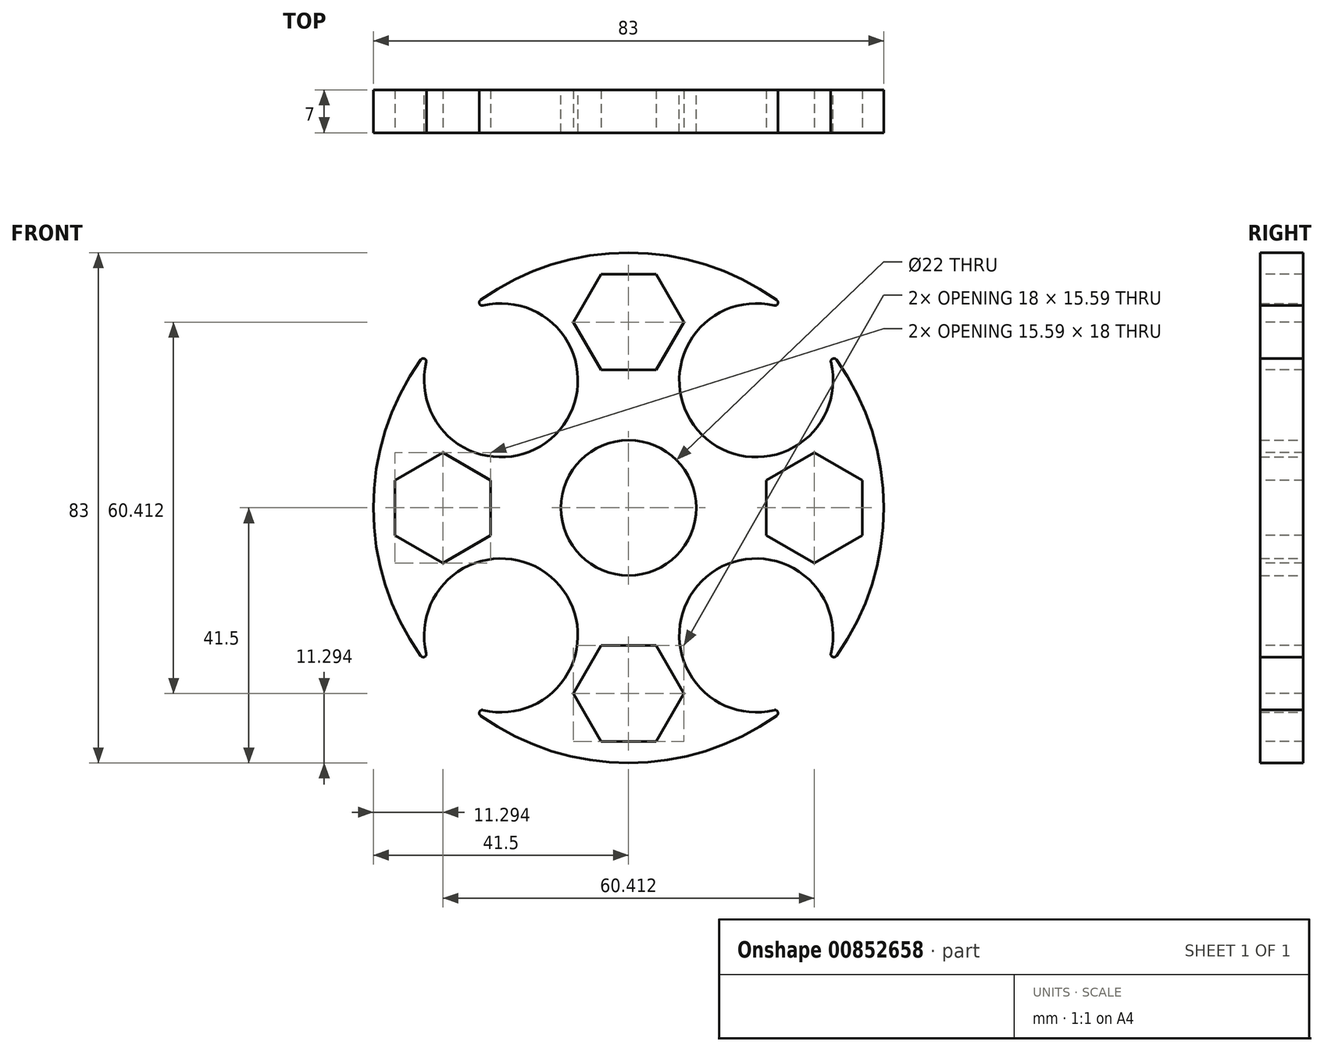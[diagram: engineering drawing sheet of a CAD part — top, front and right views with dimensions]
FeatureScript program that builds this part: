
annotation { "Feature Type Name" : "Feature", "Feature Type Description" : "" }
export const myFeature = defineFeature(function(context is Context, id is Id, definition is map)
    precondition{}
    {
        {
            var Q0;
            Q0=qCreatedBy(makeId("Front.planeOp"),FACE);
            var sketch = newSketch(context, id + "F0", { "sketchPlane" : qUnion([Q0])});
            skCircle(sketch, "E0", {"center": v(0, 0) * mm, "radius": 11 * mm});
            skCircle(sketch, "E1", {"center": v(0, 0) * mm, "radius": 41.5 * mm});
            skLineSegment(sketch, "E2", {"start": v(0, 0) * mm, "end": v(0, 41.5) * mm});
            skLineSegment(sketch, "E3", {"start": v(0, 0) * mm, "end": v(41.5, 0) * mm});
            skLineSegment(sketch, "E4", {"start": v(0, 0) * mm, "end": v(0, -41.5) * mm});
            skLineSegment(sketch, "E5", {"start": v(0, 0) * mm, "end": v(-41.5, 0) * mm});
            skLineSegment(sketch, "E6", {"start": v(-20.75, 0) * mm, "end": v(-20.75, 35.94) * mm});
            skLineSegment(sketch, "E7", {"start": v(0, 20.75) * mm, "end": v(-35.94, 20.75) * mm});
            skLineSegment(sketch, "E8", {"start": v(0, 20.75) * mm, "end": v(35.94, 20.75) * mm});
            skLineSegment(sketch, "E9", {"start": v(20.75, 0) * mm, "end": v(20.75, 35.94) * mm});
            skLineSegment(sketch, "E10", {"start": v(0, -20.75) * mm, "end": v(35.94, -20.75) * mm});
            skLineSegment(sketch, "E11", {"start": v(20.75, 0) * mm, "end": v(20.75, -35.94) * mm});
            skLineSegment(sketch, "E12", {"start": v(-20.75, 0) * mm, "end": v(-20.75, -35.94) * mm});
            skLineSegment(sketch, "E13", {"start": v(0, -20.75) * mm, "end": v(-35.94, -20.75) * mm});
            skCircle(sketch, "E14", {"center": v(-20.75, 20.75) * mm, "radius": 12.5 * mm});
            skCircle(sketch, "E15", {"center": v(20.75, 20.75) * mm, "radius": 12.5 * mm});
            skCircle(sketch, "E16", {"center": v(-20.75, -20.75) * mm, "radius": 12.5 * mm});
            skCircle(sketch, "E17", {"center": v(20.75, -20.75) * mm, "radius": 12.5 * mm});
            skSolve(sketch);
        }
        {
            var Q0;
            {var subQ1=sQuery(id+"F0.wireOp",EDGE,"E2");var subQ5=sQuery(id+"F0.wireOp",EDGE,"E1");var subQ6=makeQuery(id+"F0.imprint","INTERSECT",VERTEX,{"derivedFrom":[subQ5,subQ1]});Q0=makeQuery(id+"F0.imprint","IMPRINT",FACE,{"disambiguationData":[TD([[makeQuery(id+"F0.imprint","IMPRINT",EDGE,{"disambiguationData":[TD([[subQ6,-1.0]])],"derivedFrom":subQ5}),1.0]])]});}
            var Q1;
            {var subQ1=sQuery(id+"F0.wireOp",EDGE,"E2");var subQ7=sQuery(id+"F0.wireOp",EDGE,"E1");var subQ9=makeQuery(id+"F0.imprint","INTERSECT",VERTEX,{"derivedFrom":[subQ7,subQ1]});Q1=makeQuery(id+"F0.imprint","IMPRINT",FACE,{"disambiguationData":[TD([[makeQuery(id+"F0.imprint","IMPRINT",EDGE,{"disambiguationData":[TD([[subQ9,1.0]])],"derivedFrom":subQ7}),1.0]])]});}
            var Q2;
            {var subQ3=sQuery(id+"F0.wireOp",EDGE,"E0");var subQ5=sQuery(id+"F0.wireOp",EDGE,"E2");var subQ6=makeQuery(id+"F0.imprint","INTERSECT",VERTEX,{"derivedFrom":[subQ3,subQ5]});Q2=makeQuery(id+"F0.imprint","IMPRINT",FACE,{"disambiguationData":[TD([[makeQuery(id+"F0.imprint","IMPRINT",EDGE,{"disambiguationData":[TD([[subQ6,-1.0]])],"derivedFrom":subQ3}),-1.0]])]});}
            var Q3;
            {var subQ1=sQuery(id+"F0.wireOp",EDGE,"E2");var subQ5=sQuery(id+"F0.wireOp",EDGE,"E0");var subQ6=makeQuery(id+"F0.imprint","INTERSECT",VERTEX,{"derivedFrom":[subQ5,subQ1]});Q3=makeQuery(id+"F0.imprint","IMPRINT",FACE,{"disambiguationData":[TD([[makeQuery(id+"F0.imprint","IMPRINT",EDGE,{"disambiguationData":[TD([[subQ6,1.0]])],"derivedFrom":subQ5}),-1.0]])]});}
            var Q4;
            {var subQ1=sQuery(id+"F0.wireOp",EDGE,"E3");var subQ5=sQuery(id+"F0.wireOp",EDGE,"E1");var subQ6=makeQuery(id+"F0.imprint","INTERSECT",VERTEX,{"derivedFrom":[subQ5,subQ1]});Q4=makeQuery(id+"F0.imprint","IMPRINT",FACE,{"disambiguationData":[TD([[makeQuery(id+"F0.imprint","IMPRINT",EDGE,{"disambiguationData":[TD([[subQ6,-1.0]])],"derivedFrom":subQ5}),1.0]])]});}
            var Q5;
            {var subQ1=sQuery(id+"F0.wireOp",EDGE,"E5");var subQ5=sQuery(id+"F0.wireOp",EDGE,"E1");var subQ6=makeQuery(id+"F0.imprint","INTERSECT",VERTEX,{"derivedFrom":[subQ5,subQ1]});Q5=makeQuery(id+"F0.imprint","IMPRINT",FACE,{"disambiguationData":[TD([[makeQuery(id+"F0.imprint","IMPRINT",EDGE,{"disambiguationData":[TD([[subQ6,1.0]])],"derivedFrom":subQ5}),1.0]])]});}
            var Q6;
            {var subQ1=sQuery(id+"F0.wireOp",EDGE,"E1");var subQ6=sQuery(id+"F0.wireOp",EDGE,"E5");var subQ9=makeQuery(id+"F0.imprint","INTERSECT",VERTEX,{"derivedFrom":[subQ1,subQ6]});Q6=makeQuery(id+"F0.imprint","IMPRINT",FACE,{"disambiguationData":[TD([[makeQuery(id+"F0.imprint","IMPRINT",EDGE,{"disambiguationData":[TD([[subQ9,-1.0]])],"derivedFrom":subQ1}),1.0]])]});}
            var Q7;
            {var subQ1=sQuery(id+"F0.wireOp",EDGE,"E5");var subQ5=sQuery(id+"F0.wireOp",EDGE,"E0");var subQ6=makeQuery(id+"F0.imprint","INTERSECT",VERTEX,{"derivedFrom":[subQ5,subQ1]});Q7=makeQuery(id+"F0.imprint","IMPRINT",FACE,{"disambiguationData":[TD([[makeQuery(id+"F0.imprint","IMPRINT",EDGE,{"disambiguationData":[TD([[subQ6,-1.0]])],"derivedFrom":subQ5}),-1.0]])]});}
            var Q8;
            {var subQ1=sQuery(id+"F0.wireOp",EDGE,"E4");var subQ5=sQuery(id+"F0.wireOp",EDGE,"E1");var subQ6=makeQuery(id+"F0.imprint","INTERSECT",VERTEX,{"derivedFrom":[subQ5,subQ1]});Q8=makeQuery(id+"F0.imprint","IMPRINT",FACE,{"disambiguationData":[TD([[makeQuery(id+"F0.imprint","IMPRINT",EDGE,{"disambiguationData":[TD([[subQ6,1.0]])],"derivedFrom":subQ5}),1.0]])]});}
            var Q9;
            {var subQ1=sQuery(id+"F0.wireOp",EDGE,"E4");var subQ5=sQuery(id+"F0.wireOp",EDGE,"E1");var subQ6=makeQuery(id+"F0.imprint","INTERSECT",VERTEX,{"derivedFrom":[subQ5,subQ1]});Q9=makeQuery(id+"F0.imprint","IMPRINT",FACE,{"disambiguationData":[TD([[makeQuery(id+"F0.imprint","IMPRINT",EDGE,{"disambiguationData":[TD([[subQ6,-1.0]])],"derivedFrom":subQ5}),1.0]])]});}
            var Q10;
            {var subQ5=sQuery(id+"F0.wireOp",EDGE,"E0");var subQ8=sQuery(id+"F0.wireOp",EDGE,"E3");var subQ10=makeQuery(id+"F0.imprint","INTERSECT",VERTEX,{"derivedFrom":[subQ5,subQ8]});Q10=makeQuery(id+"F0.imprint","IMPRINT",FACE,{"disambiguationData":[TD([[makeQuery(id+"F0.imprint","IMPRINT",EDGE,{"disambiguationData":[TD([[subQ10,1.0]])],"derivedFrom":subQ5}),-1.0]])]});}
            var Q11;
            {var subQ1=sQuery(id+"F0.wireOp",EDGE,"E3");var subQ5=sQuery(id+"F0.wireOp",EDGE,"E1");var subQ6=makeQuery(id+"F0.imprint","INTERSECT",VERTEX,{"derivedFrom":[subQ5,subQ1]});Q11=makeQuery(id+"F0.imprint","IMPRINT",FACE,{"disambiguationData":[TD([[makeQuery(id+"F0.imprint","IMPRINT",EDGE,{"disambiguationData":[TD([[subQ6,1.0]])],"derivedFrom":subQ5}),1.0]])]});}
            var Q12;
            {var subQ0=sQuery(id+"F0.wireOp",EDGE,"E11");var subQ1=sQuery(id+"F0.wireOp",EDGE,"E1");var subQ2=makeQuery(id+"F0.imprint","INTERSECT",VERTEX,{"derivedFrom":[subQ1,subQ0]});Q12=makeQuery(id+"F0.imprint","IMPRINT",FACE,{"disambiguationData":[TD([[makeQuery(id+"F0.imprint","IMPRINT",EDGE,{"disambiguationData":[TD([[subQ2,-1.0]])],"derivedFrom":subQ1}),1.0]])]});}
            var Q13;
            {var subQ0=sQuery(id+"F0.wireOp",EDGE,"E10");var subQ1=sQuery(id+"F0.wireOp",EDGE,"E1");var subQ2=makeQuery(id+"F0.imprint","INTERSECT",VERTEX,{"derivedFrom":[subQ1,subQ0]});Q13=makeQuery(id+"F0.imprint","IMPRINT",FACE,{"disambiguationData":[TD([[makeQuery(id+"F0.imprint","IMPRINT",EDGE,{"disambiguationData":[TD([[subQ2,1.0]])],"derivedFrom":subQ1}),1.0]])]});}
            var Q14;
            {var subQ0=sQuery(id+"F0.wireOp",EDGE,"E12");var subQ1=sQuery(id+"F0.wireOp",EDGE,"E1");var subQ2=makeQuery(id+"F0.imprint","INTERSECT",VERTEX,{"derivedFrom":[subQ1,subQ0]});Q14=makeQuery(id+"F0.imprint","IMPRINT",FACE,{"disambiguationData":[TD([[makeQuery(id+"F0.imprint","IMPRINT",EDGE,{"disambiguationData":[TD([[subQ2,1.0]])],"derivedFrom":subQ1}),1.0]])]});}
            var Q15;
            {var subQ0=sQuery(id+"F0.wireOp",EDGE,"E13");var subQ1=sQuery(id+"F0.wireOp",EDGE,"E1");var subQ2=makeQuery(id+"F0.imprint","INTERSECT",VERTEX,{"derivedFrom":[subQ1,subQ0]});Q15=makeQuery(id+"F0.imprint","IMPRINT",FACE,{"disambiguationData":[TD([[makeQuery(id+"F0.imprint","IMPRINT",EDGE,{"disambiguationData":[TD([[subQ2,-1.0]])],"derivedFrom":subQ1}),1.0]])]});}
            var Q16;
            {var subQ0=sQuery(id+"F0.wireOp",EDGE,"E7");var subQ1=sQuery(id+"F0.wireOp",EDGE,"E1");var subQ2=makeQuery(id+"F0.imprint","INTERSECT",VERTEX,{"derivedFrom":[subQ1,subQ0]});Q16=makeQuery(id+"F0.imprint","IMPRINT",FACE,{"disambiguationData":[TD([[makeQuery(id+"F0.imprint","IMPRINT",EDGE,{"disambiguationData":[TD([[subQ2,1.0]])],"derivedFrom":subQ1}),1.0]])]});}
            var Q17;
            {var subQ0=sQuery(id+"F0.wireOp",EDGE,"E6");var subQ1=sQuery(id+"F0.wireOp",EDGE,"E1");var subQ2=makeQuery(id+"F0.imprint","INTERSECT",VERTEX,{"derivedFrom":[subQ1,subQ0]});Q17=makeQuery(id+"F0.imprint","IMPRINT",FACE,{"disambiguationData":[TD([[makeQuery(id+"F0.imprint","IMPRINT",EDGE,{"disambiguationData":[TD([[subQ2,-1.0]])],"derivedFrom":subQ1}),1.0]])]});}
            var Q18;
            {var subQ0=sQuery(id+"F0.wireOp",EDGE,"E9");var subQ1=sQuery(id+"F0.wireOp",EDGE,"E1");var subQ2=makeQuery(id+"F0.imprint","INTERSECT",VERTEX,{"derivedFrom":[subQ1,subQ0]});Q18=makeQuery(id+"F0.imprint","IMPRINT",FACE,{"disambiguationData":[TD([[makeQuery(id+"F0.imprint","IMPRINT",EDGE,{"disambiguationData":[TD([[subQ2,1.0]])],"derivedFrom":subQ1}),1.0]])]});}
            var Q19;
            {var subQ0=sQuery(id+"F0.wireOp",EDGE,"E8");var subQ1=sQuery(id+"F0.wireOp",EDGE,"E1");var subQ2=makeQuery(id+"F0.imprint","INTERSECT",VERTEX,{"derivedFrom":[subQ1,subQ0]});Q19=makeQuery(id+"F0.imprint","IMPRINT",FACE,{"disambiguationData":[TD([[makeQuery(id+"F0.imprint","IMPRINT",EDGE,{"disambiguationData":[TD([[subQ2,-1.0]])],"derivedFrom":subQ1}),1.0]])]});}
            extrude(context, id + "F1", {"entities" : qUnion([Q0, Q1, Q2, Q3, Q4, Q5, Q6, Q7, Q8, Q9, Q10, Q11, Q12, Q13, Q14, Q15, Q16, Q17, Q18, Q19]), "depth" : 7 * mm, "offsetDistance" : 25 * mm});
        }
        {
            var Q0;
            {var subQ0=sQuery(id+"F0.wireOp",EDGE,"E15");var subQ1=sQuery(id+"F0.wireOp",EDGE,"E1");Q0=makeQuery(id+"F1.opExtrude","SWEPT_EDGE",EDGE,{"disambiguationData":[OSD([subQ1,subQ0]),TDD([makeQuery(id+"F0.imprint","INTERSECT",VERTEX,{"disambiguationData":[OD(1.0)],"derivedFrom":[subQ1,subQ0]})])]});}
            var Q1;
            {var subQ0=sQuery(id+"F0.wireOp",EDGE,"E15");var subQ1=sQuery(id+"F0.wireOp",EDGE,"E1");Q1=makeQuery(id+"F1.opExtrude","SWEPT_EDGE",EDGE,{"disambiguationData":[OSD([subQ1,subQ0]),TDD([makeQuery(id+"F0.imprint","INTERSECT",VERTEX,{"disambiguationData":[OD(0.0)],"derivedFrom":[subQ1,subQ0]})])]});}
            var Q2;
            {var subQ0=sQuery(id+"F0.wireOp",EDGE,"E17");var subQ1=sQuery(id+"F0.wireOp",EDGE,"E1");Q2=makeQuery(id+"F1.opExtrude","SWEPT_EDGE",EDGE,{"disambiguationData":[OSD([subQ1,subQ0]),TDD([makeQuery(id+"F0.imprint","INTERSECT",VERTEX,{"disambiguationData":[OD(1.0)],"derivedFrom":[subQ1,subQ0]})])]});}
            var Q3;
            {var subQ0=sQuery(id+"F0.wireOp",EDGE,"E17");var subQ1=sQuery(id+"F0.wireOp",EDGE,"E1");Q3=makeQuery(id+"F1.opExtrude","SWEPT_EDGE",EDGE,{"disambiguationData":[OSD([subQ1,subQ0]),TDD([makeQuery(id+"F0.imprint","INTERSECT",VERTEX,{"disambiguationData":[OD(0.0)],"derivedFrom":[subQ1,subQ0]})])]});}
            var Q4;
            {var subQ0=sQuery(id+"F0.wireOp",EDGE,"E16");var subQ1=sQuery(id+"F0.wireOp",EDGE,"E1");Q4=makeQuery(id+"F1.opExtrude","SWEPT_EDGE",EDGE,{"disambiguationData":[OSD([subQ1,subQ0]),TDD([makeQuery(id+"F0.imprint","INTERSECT",VERTEX,{"disambiguationData":[OD(1.0)],"derivedFrom":[subQ1,subQ0]})])]});}
            var Q5;
            {var subQ0=sQuery(id+"F0.wireOp",EDGE,"E16");var subQ1=sQuery(id+"F0.wireOp",EDGE,"E1");Q5=makeQuery(id+"F1.opExtrude","SWEPT_EDGE",EDGE,{"disambiguationData":[OSD([subQ1,subQ0]),TDD([makeQuery(id+"F0.imprint","INTERSECT",VERTEX,{"disambiguationData":[OD(0.0)],"derivedFrom":[subQ1,subQ0]})])]});}
            var Q6;
            {var subQ0=sQuery(id+"F0.wireOp",EDGE,"E14");var subQ1=sQuery(id+"F0.wireOp",EDGE,"E1");Q6=makeQuery(id+"F1.opExtrude","SWEPT_EDGE",EDGE,{"disambiguationData":[OSD([subQ1,subQ0]),TDD([makeQuery(id+"F0.imprint","INTERSECT",VERTEX,{"disambiguationData":[OD(0.0)],"derivedFrom":[subQ1,subQ0]})])]});}
            var Q7;
            {var subQ0=sQuery(id+"F0.wireOp",EDGE,"E14");var subQ1=sQuery(id+"F0.wireOp",EDGE,"E1");Q7=makeQuery(id+"F1.opExtrude","SWEPT_EDGE",EDGE,{"disambiguationData":[OSD([subQ1,subQ0]),TDD([makeQuery(id+"F0.imprint","INTERSECT",VERTEX,{"disambiguationData":[OD(1.0)],"derivedFrom":[subQ1,subQ0]})])]});}
            fillet(context, id + "F2", {"entities" : qUnion([Q0, Q1, Q2, Q3, Q4, Q5, Q6, Q7]), "radius" : 0.5 * mm, "tangentPropagation" : true, "allowEdgeOverflow" : false});
        }
        {
            var Q0;
            Q0=makeQuery(id+"F1.opExtrude","CAP_FACE",FACE,{"disambiguationData":[OSD([sQuery(id+"F0.wireOp",EDGE,"E0"),sQuery(id+"F0.wireOp",EDGE,"E1"),sQuery(id+"F0.wireOp",EDGE,"E14"),sQuery(id+"F0.wireOp",EDGE,"E15"),sQuery(id+"F0.wireOp",EDGE,"E16"),sQuery(id+"F0.wireOp",EDGE,"E17")])],"isStart":false});
            var sketch = newSketch(context, id + "F3", { "sketchPlane" : qUnion([Q0])});
            skLineSegment(sketch, "E18", {"start": v(-4.5, 38) * mm, "end": v(4.5, 38) * mm});
            skLineSegment(sketch, "E19", {"start": v(4.5, 38) * mm, "end": v(9, 30.2) * mm});
            skLineSegment(sketch, "E20", {"start": v(9, 30.2) * mm, "end": v(4.5, 22.41) * mm});
            skLineSegment(sketch, "E21", {"start": v(4.5, 22.41) * mm, "end": v(-4.5, 22.41) * mm});
            skLineSegment(sketch, "E22", {"start": v(-4.5, 22.41) * mm, "end": v(-9, 30.2) * mm});
            skLineSegment(sketch, "E23", {"start": v(-9, 30.2) * mm, "end": v(-4.5, 38) * mm});
            skLineSegment(sketch, "E24", {"start": v(0, 38) * mm, "end": v(0, 22.41) * mm});
            skLineSegment(sketch, "E25", {"start": v(38, 4.5) * mm, "end": v(38, -4.5) * mm});
            skLineSegment(sketch, "E26", {"start": v(38, -4.5) * mm, "end": v(30.2, -9) * mm});
            skLineSegment(sketch, "E27", {"start": v(30.2, -9) * mm, "end": v(22.41, -4.5) * mm});
            skLineSegment(sketch, "E28", {"start": v(22.41, -4.5) * mm, "end": v(22.41, 4.5) * mm});
            skLineSegment(sketch, "E29", {"start": v(22.41, 4.5) * mm, "end": v(30.2, 9) * mm});
            skLineSegment(sketch, "E30", {"start": v(30.2, 9) * mm, "end": v(38, 4.5) * mm});
            skLineSegment(sketch, "E31", {"start": v(38, 0) * mm, "end": v(22.41, 0) * mm});
            skLineSegment(sketch, "E32", {"start": v(-22.41, 4.5) * mm, "end": v(-22.41, -4.5) * mm});
            skLineSegment(sketch, "E33", {"start": v(-22.41, -4.5) * mm, "end": v(-30.2, -9) * mm});
            skLineSegment(sketch, "E34", {"start": v(-30.2, -9) * mm, "end": v(-38, -4.5) * mm});
            skLineSegment(sketch, "E35", {"start": v(-38, -4.5) * mm, "end": v(-38, 4.5) * mm});
            skLineSegment(sketch, "E36", {"start": v(-38, 4.5) * mm, "end": v(-30.2, 9) * mm});
            skLineSegment(sketch, "E37", {"start": v(-30.2, 9) * mm, "end": v(-22.41, 4.5) * mm});
            skLineSegment(sketch, "E38", {"start": v(-22.41, 0) * mm, "end": v(-38, 0) * mm});
            skLineSegment(sketch, "E39", {"start": v(-4.5, -22.41) * mm, "end": v(4.5, -22.41) * mm});
            skLineSegment(sketch, "E40", {"start": v(4.5, -22.41) * mm, "end": v(9, -30.2) * mm});
            skLineSegment(sketch, "E41", {"start": v(9, -30.2) * mm, "end": v(4.5, -38) * mm});
            skLineSegment(sketch, "E42", {"start": v(4.5, -38) * mm, "end": v(-4.5, -38) * mm});
            skLineSegment(sketch, "E43", {"start": v(-4.5, -38) * mm, "end": v(-9, -30.2) * mm});
            skLineSegment(sketch, "E44", {"start": v(-9, -30.2) * mm, "end": v(-4.5, -22.41) * mm});
            skLineSegment(sketch, "E45", {"start": v(0, -22.41) * mm, "end": v(0, -38) * mm});
            skSolve(sketch);
        }
        {
            var Q0;
            {var subQ1=sQuery(id+"F3.wireOp",EDGE,"E36");Q0=makeQuery(id+"F3.imprint","IMPRINT",FACE,{"disambiguationData":[TD([[makeQuery(id+"F3.imprint","IMPRINT",EDGE,{"derivedFrom":subQ1}),-1.0]])]});}
            var Q1;
            {var subQ3=sQuery(id+"F3.wireOp",EDGE,"E33");Q1=makeQuery(id+"F3.imprint","IMPRINT",FACE,{"disambiguationData":[TD([[makeQuery(id+"F3.imprint","IMPRINT",EDGE,{"derivedFrom":subQ3}),-1.0]])]});}
            var Q2;
            {var subQ1=sQuery(id+"F3.wireOp",EDGE,"E22");Q2=makeQuery(id+"F3.imprint","IMPRINT",FACE,{"disambiguationData":[TD([[makeQuery(id+"F3.imprint","IMPRINT",EDGE,{"derivedFrom":subQ1}),-1.0]])]});}
            var Q3;
            {var subQ3=sQuery(id+"F3.wireOp",EDGE,"E19");Q3=makeQuery(id+"F3.imprint","IMPRINT",FACE,{"disambiguationData":[TD([[makeQuery(id+"F3.imprint","IMPRINT",EDGE,{"derivedFrom":subQ3}),-1.0]])]});}
            var Q4;
            {var subQ1=sQuery(id+"F3.wireOp",EDGE,"E29");Q4=makeQuery(id+"F3.imprint","IMPRINT",FACE,{"disambiguationData":[TD([[makeQuery(id+"F3.imprint","IMPRINT",EDGE,{"derivedFrom":subQ1}),-1.0]])]});}
            var Q5;
            {var subQ3=sQuery(id+"F3.wireOp",EDGE,"E26");Q5=makeQuery(id+"F3.imprint","IMPRINT",FACE,{"disambiguationData":[TD([[makeQuery(id+"F3.imprint","IMPRINT",EDGE,{"derivedFrom":subQ3}),-1.0]])]});}
            var Q6;
            {var subQ1=sQuery(id+"F3.wireOp",EDGE,"E43");Q6=makeQuery(id+"F3.imprint","IMPRINT",FACE,{"disambiguationData":[TD([[makeQuery(id+"F3.imprint","IMPRINT",EDGE,{"derivedFrom":subQ1}),-1.0]])]});}
            var Q7;
            {var subQ3=sQuery(id+"F3.wireOp",EDGE,"E40");Q7=makeQuery(id+"F3.imprint","IMPRINT",FACE,{"disambiguationData":[TD([[makeQuery(id+"F3.imprint","IMPRINT",EDGE,{"derivedFrom":subQ3}),-1.0]])]});}
            extrude(context, id + "F4", {"entities" : qUnion([Q0, Q1, Q2, Q3, Q4, Q5, Q6, Q7]), "operationType" : NewBodyOperationType.REMOVE, "oppositeDirection" : true, "depth" : 25 * mm, "offsetDistance" : 25 * mm});
        }
    });
